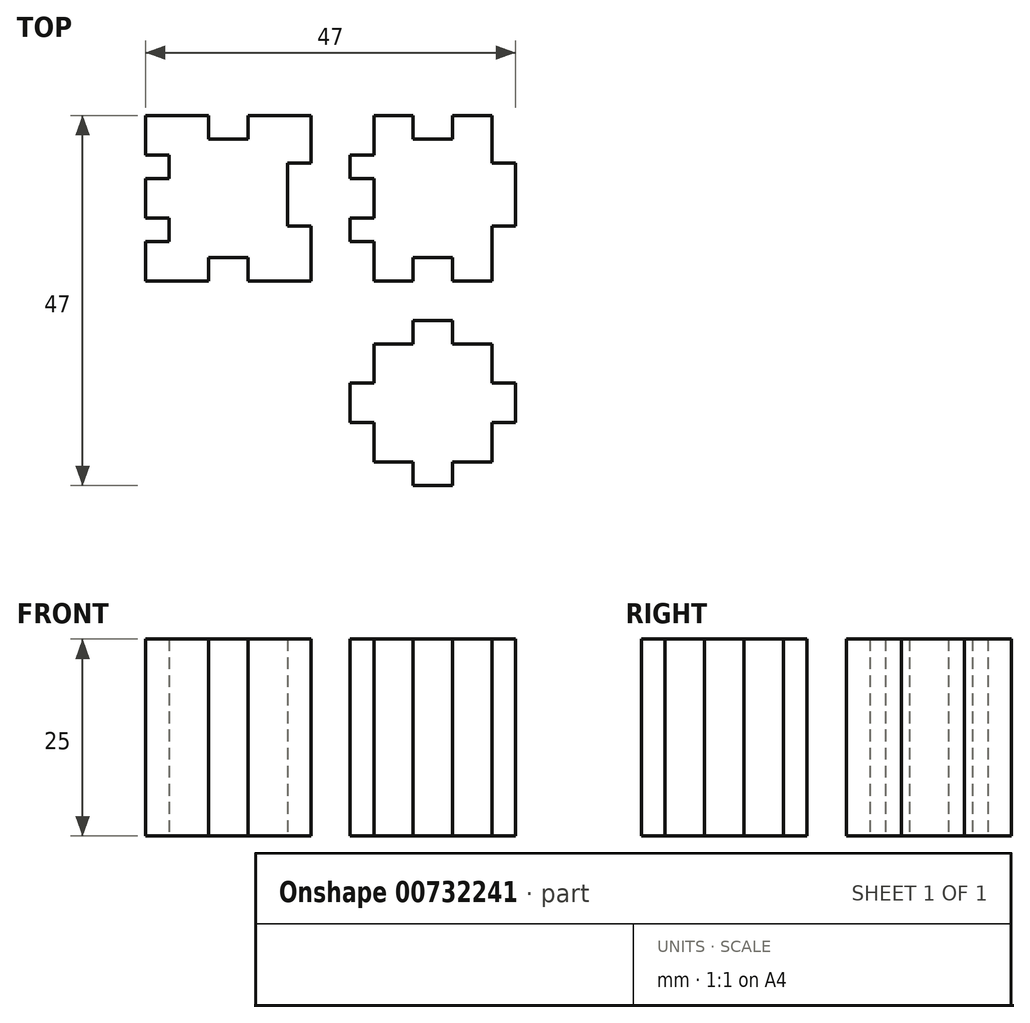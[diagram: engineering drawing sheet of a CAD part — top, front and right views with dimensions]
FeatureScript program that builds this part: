
annotation { "Feature Type Name" : "Feature", "Feature Type Description" : "" }
export const myFeature = defineFeature(function(context is Context, id is Id, definition is map)
    precondition{}
    {
        {
            var Q0;
            Q0=qCreatedBy(makeId("Top.planeOp"),FACE);
            var sketch = newSketch(context, id + "F0", { "sketchPlane" : qUnion([Q0])});
            skLineSegment(sketch, "E0", {"start": v(-23.5, 10.5) * mm, "end": v(-23.5, 5.5) * mm});
            skLineSegment(sketch, "E1", {"start": v(-23.5, 5.5) * mm, "end": v(-20.5, 5.5) * mm});
            skLineSegment(sketch, "E2", {"start": v(-20.5, 5.5) * mm, "end": v(-20.5, 2.5) * mm});
            skLineSegment(sketch, "E3", {"start": v(-20.5, 2.5) * mm, "end": v(-23.5, 2.5) * mm});
            skLineSegment(sketch, "E4", {"start": v(-23.5, 2.5) * mm, "end": v(-23.5, -2.5) * mm});
            skLineSegment(sketch, "E5", {"start": v(-23.5, -2.5) * mm, "end": v(-20.5, -2.5) * mm});
            skLineSegment(sketch, "E6", {"start": v(-20.5, -2.5) * mm, "end": v(-20.5, -5.5) * mm});
            skLineSegment(sketch, "E7", {"start": v(-20.5, -5.5) * mm, "end": v(-23.5, -5.5) * mm});
            skLineSegment(sketch, "E8", {"start": v(-23.5, -5.5) * mm, "end": v(-23.5, -10.5) * mm});
            skLineSegment(sketch, "E9", {"start": v(-2.5, -10.5) * mm, "end": v(-2.5, -3.5) * mm});
            skLineSegment(sketch, "E10", {"start": v(-2.5, -3.5) * mm, "end": v(-5.5, -3.5) * mm});
            skLineSegment(sketch, "E11", {"start": v(-5.5, -3.5) * mm, "end": v(-5.5, 4.5) * mm});
            skLineSegment(sketch, "E12", {"start": v(-5.5, 4.5) * mm, "end": v(-2.5, 4.5) * mm});
            skLineSegment(sketch, "E13", {"start": v(-2.5, 4.5) * mm, "end": v(-2.5, 10.5) * mm});
            skLineSegment(sketch, "E14", {"start": v(5.5, 10.5) * mm, "end": v(5.5, 5.5) * mm});
            skLineSegment(sketch, "E15", {"start": v(5.5, 5.5) * mm, "end": v(2.5, 5.5) * mm});
            skLineSegment(sketch, "E16", {"start": v(2.5, 5.5) * mm, "end": v(2.5, 2.5) * mm});
            skLineSegment(sketch, "E17", {"start": v(2.5, 2.5) * mm, "end": v(5.5, 2.5) * mm});
            skLineSegment(sketch, "E18", {"start": v(5.5, 2.5) * mm, "end": v(5.5, -2.5) * mm});
            skLineSegment(sketch, "E19", {"start": v(5.5, -2.5) * mm, "end": v(2.5, -2.5) * mm});
            skLineSegment(sketch, "E20", {"start": v(2.5, -2.5) * mm, "end": v(2.5, -5.5) * mm});
            skLineSegment(sketch, "E21", {"start": v(2.5, -5.5) * mm, "end": v(5.5, -5.5) * mm});
            skLineSegment(sketch, "E22", {"start": v(5.5, -5.5) * mm, "end": v(5.5, -10.5) * mm});
            skLineSegment(sketch, "E23", {"start": v(20.5, -10.5) * mm, "end": v(20.5, -3.5) * mm});
            skLineSegment(sketch, "E24", {"start": v(20.5, -3.5) * mm, "end": v(23.5, -3.5) * mm});
            skLineSegment(sketch, "E25", {"start": v(23.5, -3.5) * mm, "end": v(23.5, 4.5) * mm});
            skLineSegment(sketch, "E26", {"start": v(23.5, 4.5) * mm, "end": v(20.5, 4.5) * mm});
            skLineSegment(sketch, "E27", {"start": v(20.5, 4.5) * mm, "end": v(20.5, 10.5) * mm});
            skLineSegment(sketch, "E28", {"start": v(-15.5, 10.5) * mm, "end": v(-15.5, 7.5) * mm});
            skLineSegment(sketch, "E29", {"start": v(-15.5, 7.5) * mm, "end": v(-10.5, 7.5) * mm});
            skLineSegment(sketch, "E30", {"start": v(-10.5, 7.5) * mm, "end": v(-10.5, 10.5) * mm});
            skLineSegment(sketch, "E31", {"start": v(-23.5, 10.5) * mm, "end": v(-15.5, 10.5) * mm});
            skLineSegment(sketch, "E32", {"start": v(-10.5, 10.5) * mm, "end": v(-2.5, 10.5) * mm});
            skLineSegment(sketch, "E33", {"start": v(10.5, 10.5) * mm, "end": v(10.5, 7.5) * mm});
            skLineSegment(sketch, "E34", {"start": v(10.5, 7.5) * mm, "end": v(15.5, 7.5) * mm});
            skLineSegment(sketch, "E35", {"start": v(15.5, 7.5) * mm, "end": v(15.5, 10.5) * mm});
            skLineSegment(sketch, "E36", {"start": v(5.5, 10.5) * mm, "end": v(10.5, 10.5) * mm});
            skLineSegment(sketch, "E37", {"start": v(15.5, 10.5) * mm, "end": v(20.5, 10.5) * mm});
            skLineSegment(sketch, "E38", {"start": v(-15.5, -10.5) * mm, "end": v(-15.5, -7.5) * mm});
            skLineSegment(sketch, "E39", {"start": v(-15.5, -7.5) * mm, "end": v(-10.5, -7.5) * mm});
            skLineSegment(sketch, "E40", {"start": v(-10.5, -7.5) * mm, "end": v(-10.5, -10.5) * mm});
            skLineSegment(sketch, "E41", {"start": v(-23.5, -10.5) * mm, "end": v(-15.5, -10.5) * mm});
            skLineSegment(sketch, "E42", {"start": v(-10.5, -10.5) * mm, "end": v(-2.5, -10.5) * mm});
            skLineSegment(sketch, "E43", {"start": v(10.5, -10.5) * mm, "end": v(10.5, -7.5) * mm});
            skPoint(sketch, "E43.endSnap0", {"position": v(-13, -7.5) * mm});
            skLineSegment(sketch, "E44", {"start": v(10.5, -7.5) * mm, "end": v(15.5, -7.5) * mm});
            skLineSegment(sketch, "E45", {"start": v(15.5, -7.5) * mm, "end": v(15.5, -10.5) * mm});
            skLineSegment(sketch, "E46", {"start": v(5.5, -10.5) * mm, "end": v(10.5, -10.5) * mm});
            skLineSegment(sketch, "E47", {"start": v(15.5, -10.5) * mm, "end": v(20.5, -10.5) * mm});
            skLineSegment(sketch, "E48", {"start": v(5.5, -18.5) * mm, "end": v(10.5, -18.5) * mm});
            skLineSegment(sketch, "E49", {"start": v(10.5, -18.5) * mm, "end": v(10.5, -15.5) * mm});
            skLineSegment(sketch, "E50", {"start": v(10.5, -15.5) * mm, "end": v(15.5, -15.5) * mm});
            skLineSegment(sketch, "E51", {"start": v(15.5, -15.5) * mm, "end": v(15.5, -18.5) * mm});
            skLineSegment(sketch, "E52", {"start": v(15.5, -18.5) * mm, "end": v(20.5, -18.5) * mm});
            skLineSegment(sketch, "E53", {"start": v(20.5, -18.5) * mm, "end": v(20.5, -23.5) * mm});
            skLineSegment(sketch, "E54", {"start": v(20.5, -23.5) * mm, "end": v(23.5, -23.5) * mm});
            skLineSegment(sketch, "E55", {"start": v(23.5, -23.5) * mm, "end": v(23.5, -28.5) * mm});
            skLineSegment(sketch, "E56", {"start": v(23.5, -28.5) * mm, "end": v(20.5, -28.5) * mm});
            skLineSegment(sketch, "E57", {"start": v(20.5, -28.5) * mm, "end": v(20.5, -33.5) * mm});
            skLineSegment(sketch, "E58", {"start": v(20.5, -33.5) * mm, "end": v(15.5, -33.5) * mm});
            skLineSegment(sketch, "E59", {"start": v(15.5, -33.5) * mm, "end": v(15.5, -36.5) * mm});
            skLineSegment(sketch, "E60", {"start": v(15.5, -36.5) * mm, "end": v(10.5, -36.5) * mm});
            skLineSegment(sketch, "E61", {"start": v(10.5, -36.5) * mm, "end": v(10.5, -33.5) * mm});
            skLineSegment(sketch, "E62", {"start": v(10.5, -33.5) * mm, "end": v(5.5, -33.5) * mm});
            skLineSegment(sketch, "E63", {"start": v(5.5, -33.5) * mm, "end": v(5.5, -28.5) * mm});
            skLineSegment(sketch, "E64", {"start": v(5.5, -28.5) * mm, "end": v(2.5, -28.5) * mm});
            skLineSegment(sketch, "E65", {"start": v(2.5, -28.5) * mm, "end": v(2.5, -23.5) * mm});
            skLineSegment(sketch, "E66", {"start": v(2.5, -23.5) * mm, "end": v(5.5, -23.5) * mm});
            skLineSegment(sketch, "E67", {"start": v(5.5, -23.5) * mm, "end": v(5.5, -18.5) * mm});
            skSolve(sketch);
        }
        {
            var Q0;
            Q0=makeQuery(id+"F0.imprint","IMPRINT",FACE,{"disambiguationData":[TD([[makeQuery(id+"F0.imprint","IMPRINT",EDGE,{"derivedFrom":sQuery(id+"F0.wireOp",EDGE,"IZLdT2ng-BEDQ-ll1O-Kfpm-4n0ox1U89xMS")}),1.0]])]});
            var Q1;
            Q1=makeQuery(id+"F0.imprint","IMPRINT",FACE,{"disambiguationData":[TD([[makeQuery(id+"F0.imprint","IMPRINT",EDGE,{"derivedFrom":sQuery(id+"F0.wireOp",EDGE,"E14")}),1.0]])]});
            var Q2;
            Q2=makeQuery(id+"F0.imprint","IMPRINT",FACE,{"disambiguationData":[TD([[makeQuery(id+"F0.imprint","IMPRINT",EDGE,{"derivedFrom":sQuery(id+"F0.wireOp",EDGE,"E0")}),1.0]])]});
            var Q3;
            Q3=makeQuery(id+"F0.imprint","IMPRINT",FACE,{"disambiguationData":[TD([[makeQuery(id+"F0.imprint","IMPRINT",EDGE,{"derivedFrom":sQuery(id+"F0.wireOp",EDGE,"E48")}),-1.0]])]});
            extrude(context, id + "F1", {"entities" : qUnion([Q0, Q1, Q2, Q3]), "depth" : 25 * mm, "offsetDistance" : 25 * mm});
        }
    });
